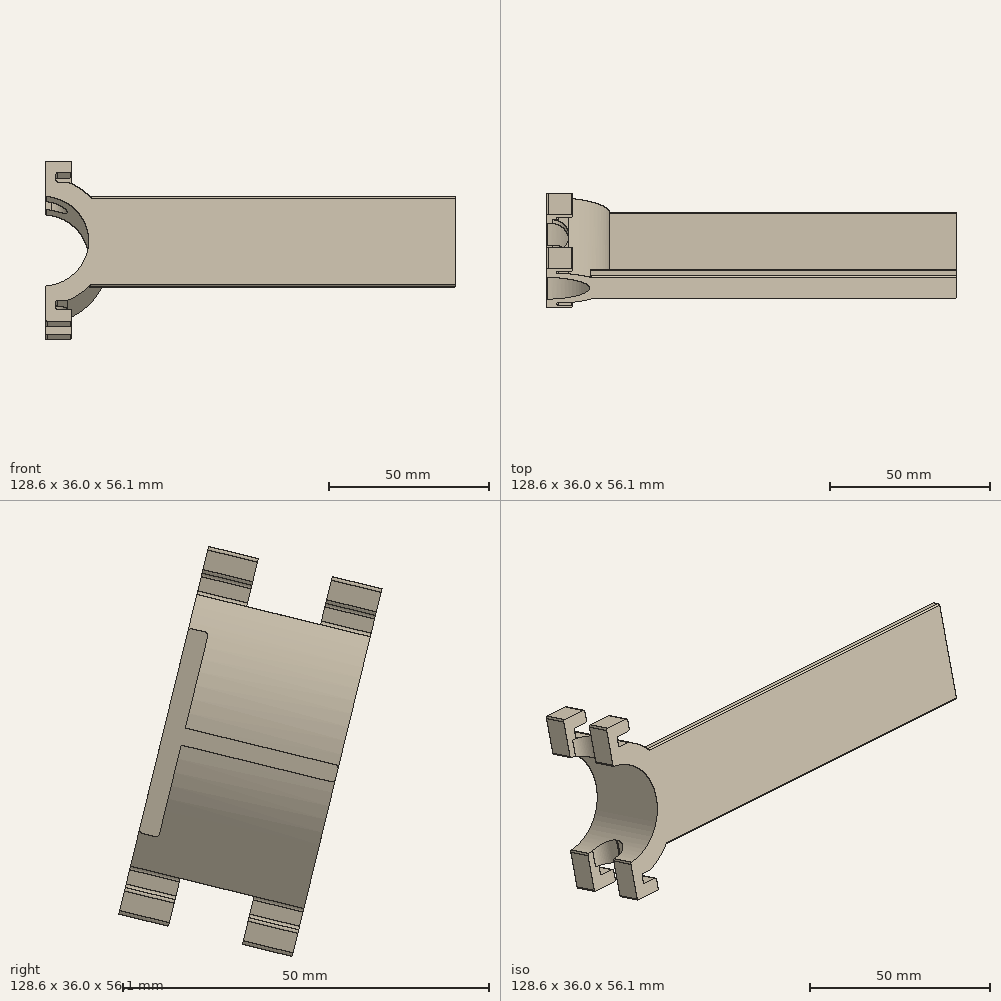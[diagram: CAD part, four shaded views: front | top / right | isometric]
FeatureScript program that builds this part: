
annotation { "Feature Type Name" : "Feature", "Feature Type Description" : "" }
export const myFeature = defineFeature(function(context is Context, id is Id, definition is map)
    precondition{}
    {
        {
            var Q0;
            Q0=qCreatedBy(makeId("Right.planeOp"),FACE);
            var sketch = newSketch(context, id + "F0", { "sketchPlane" : qUnion([Q0])});
            skLineSegment(sketch, "E0.0", {"start": v(15.97, -2.87) * mm, "end": v(15.4, -5.2) * mm});
            skLineSegment(sketch, "E0.1", {"start": v(15.4, -5.2) * mm, "end": v(-5.58, -0.08) * mm});
            skLineSegment(sketch, "E0.2", {"start": v(15.97, -2.87) * mm, "end": v(-5, 2.25) * mm});
            skLineSegment(sketch, "E0.3", {"start": v(-5.58, -0.08) * mm, "end": v(-8.66, -12.7) * mm});
            skLineSegment(sketch, "E0.4", {"start": v(-11.38, -12.04) * mm, "end": v(-8.66, -12.7) * mm});
            skLineSegment(sketch, "E0.5", {"start": v(-8.32, 0.49) * mm, "end": v(-11.38, -12.04) * mm});
            skLineSegment(sketch, "E0.6", {"start": v(-1.83, 15.27) * mm, "end": v(-5, 2.25) * mm});
            skLineSegment(sketch, "E0.7", {"start": v(-4.55, 15.93) * mm, "end": v(-1.83, 15.27) * mm});
            skLineSegment(sketch, "E0.8", {"start": v(-4.55, 15.93) * mm, "end": v(-7.6, 3.4) * mm});
            skLineSegment(sketch, "E0.9", {"start": v(-7.6, 3.4) * mm, "end": v(-8.32, 0.49) * mm});
            skSolve(sketch);
        }
        {
            var Q0;
            Q0=makeQuery(id+"F0.imprint","IMPRINT",FACE,{"disambiguationData":[TD([[makeQuery(id+"F0.imprint","IMPRINT",EDGE,{"derivedFrom":sQuery(id+"F0.wireOp",EDGE,"19673f29-938b-42fe-a6ce-3b0a3df10b1a.0")}),1.0]])]});
            var Q1;
            Q1=makeQuery(id+"F0.imprint","IMPRINT",FACE,{"disambiguationData":[TD([[makeQuery(id+"F0.imprint","IMPRINT",EDGE,{"derivedFrom":sQuery(id+"F0.wireOp",EDGE,"E0.0")}),-1.0]])]});
            extrude(context, id + "F1", {"entities" : qUnion([Q0, Q1]), "oppositeDirection" : true, "depth" : 115 * mm});
        }
        {
            var Q0;
            Q0=makeQuery(id+"F1.opExtrude","SWEPT_EDGE",EDGE,{"disambiguationData":[OSD([sQuery(id+"F0.wireOp",EDGE,"E0.0"),sQuery(id+"F0.wireOp",EDGE,"E0.1")])]});
            var Q1;
            Q1=makeQuery(id+"F1.opExtrude","SWEPT_EDGE",EDGE,{"disambiguationData":[OSD([sQuery(id+"F0.wireOp",EDGE,"E0.3"),sQuery(id+"F0.wireOp",EDGE,"E0.4")])]});
            var Q2;
            Q2=makeQuery(id+"F1.opExtrude","SWEPT_EDGE",EDGE,{"disambiguationData":[OSD([sQuery(id+"F0.wireOp",EDGE,"E0.4"),sQuery(id+"F0.wireOp",EDGE,"E0.5")])]});
            var Q3;
            Q3=makeQuery(id+"F1.opExtrude","SWEPT_EDGE",EDGE,{"disambiguationData":[OSD([sQuery(id+"F0.wireOp",EDGE,"E0.7"),sQuery(id+"F0.wireOp",EDGE,"E0.8")])]});
            var Q4;
            Q4=makeQuery(id+"F1.opExtrude","SWEPT_EDGE",EDGE,{"disambiguationData":[OSD([sQuery(id+"F0.wireOp",EDGE,"E0.6"),sQuery(id+"F0.wireOp",EDGE,"E0.7")])]});
            var Q5;
            Q5=makeQuery(id+"F1.opExtrude","SWEPT_EDGE",EDGE,{"disambiguationData":[OSD([sQuery(id+"F0.wireOp",EDGE,"E0.0"),sQuery(id+"F0.wireOp",EDGE,"E0.2")])]});
            fillet(context, id + "F2", {"entities" : qUnion([Q0, Q1, Q2, Q3, Q4, Q5]), "radius" : 0.5 * mm, "tangentPropagation" : true, "allowEdgeOverflow" : false});
        }
        {
            var Q0;
            Q0=makeQuery(id+"F1.opExtrude","SWEPT_FACE",FACE,{"disambiguationData":[OSD([sQuery(id+"F0.wireOp",EDGE,"E0.5"),sQuery(id+"F0.wireOp",EDGE,"E0.8"),sQuery(id+"F0.wireOp",EDGE,"E0.9")])]});
            var sketch = newSketch(context, id + "F3", { "sketchPlane" : qUnion([Q0])});
            skArc(sketch, "E1", {"start": v(-128.56, -14.47) * mm, "mid": v(-115, 0) * mm, "end": v(-128.56, 14.47) * mm});
            skPoint(sketch, "E1.centerSnap0", {"position": v(-115, 0) * mm});
            skLineSegment(sketch, "E2.right", {"start": v(-128.56, 25.87) * mm, "end": v(-128.56, 14.47) * mm});
            skLineSegment(sketch, "E3", {"start": v(-128.56, 25.87) * mm, "end": v(-120.27, 25.87) * mm});
            skLineSegment(sketch, "E4", {"start": v(-121.58, 19.12) * mm, "end": v(-125.27, 19.12) * mm});
            skLineSegment(sketch, "E5", {"start": v(-125.27, 19.12) * mm, "end": v(-125.27, 22.12) * mm});
            skLineSegment(sketch, "E6", {"start": v(-125.27, 22.12) * mm, "end": v(-120.27, 22.12) * mm});
            skLineSegment(sketch, "E7", {"start": v(-120.27, 25.87) * mm, "end": v(-120.27, 22.12) * mm});
            skLineSegment(sketch, "E8.MirrorCS", {"start": v(-125.27, -19.12) * mm, "end": v(-125.27, -22.12) * mm});
            skLineSegment(sketch, "E9.MirrorCS", {"start": v(-121.58, -19.12) * mm, "end": v(-125.27, -19.12) * mm});
            skLineSegment(sketch, "E10.MirrorCS", {"start": v(-120.27, -25.87) * mm, "end": v(-120.27, -22.12) * mm});
            skLineSegment(sketch, "E11.MirrorCS", {"start": v(-125.27, -22.12) * mm, "end": v(-120.27, -22.12) * mm});
            skLineSegment(sketch, "E12.MirrorCS", {"start": v(-128.56, -25.87) * mm, "end": v(-120.27, -25.87) * mm});
            skArc(sketch, "E13.trimOffspring", {"start": v(-121.58, -19.12) * mm, "mid": v(-108.8, 0) * mm, "end": v(-121.58, 19.12) * mm});
            skLineSegment(sketch, "E14.trimOffspring", {"start": v(-128.56, -14.47) * mm, "end": v(-128.56, -25.87) * mm});
            skSolve(sketch);
        }
        {
            var Q0;
            {var subQ1=sQuery(id+"F3.wireOp",EDGE,"E2.right");Q0=makeQuery(id+"F3.imprint","IMPRINT",FACE,{"disambiguationData":[TD([[makeQuery(id+"F3.imprint","IMPRINT",EDGE,{"derivedFrom":subQ1}),1.0]])]});}
            var Q1;
            {var subQ0=sQuery(id+"F0.wireOp",EDGE,"E0.9");var subQ1=sQuery(id+"F0.wireOp",EDGE,"E0.8");var subQ2=sQuery(id+"F0.wireOp",EDGE,"E0.5");var subQ4=makeQuery(id+"F1.opExtrude","SWEPT_FACE",FACE,{"disambiguationData":[OSD([subQ2,subQ1,subQ0])]});var subQ5=makeQuery(id+"F2.opFillet","BLEND_EDGE",EDGE,{"blendedFrom":[makeQuery(id+"F1.opExtrude","SWEPT_EDGE",EDGE,{"disambiguationData":[OSD([sQuery(id+"F0.wireOp",EDGE,"E0.4"),subQ2])]}),subQ4],"blendedInto":[subQ4]});var subQ10=sQuery(id+"F3.wireOp",EDGE,"E13.trimOffspring");var subQ12=makeQuery(id+"F3.imprint","INTERSECT",VERTEX,{"derivedFrom":[subQ5,subQ10]});Q1=makeQuery(id+"F3.imprint","IMPRINT",FACE,{"disambiguationData":[TD([[makeQuery(id+"F3.imprint","IMPRINT",EDGE,{"disambiguationData":[TD([[subQ12,-1.0]])],"derivedFrom":subQ10}),1.0]])]});}
            var Q2;
            Q2=makeQuery(id+"F3.imprint","IMPRINT",FACE,{"disambiguationData":[TD([[makeQuery(id+"F3.imprint","IMPRINT",EDGE,{"derivedFrom":sQuery(id+"F3.wireOp",EDGE,"E8.MirrorCS")}),-1.0]])]});
            extrude(context, id + "F4", {"entities" : qUnion([Q0, Q1, Q2]), "operationType" : NewBodyOperationType.ADD, "oppositeDirection" : true, "depth" : 24.4 * mm});
        }
        {
            var Q0;
            Q0=makeQuery(id+"F4.opExtrude","SWEPT_EDGE",EDGE,{"disambiguationData":[OSD([sQuery(id+"F3.wireOp",EDGE,"E3"),sQuery(id+"F3.wireOp",EDGE,"E7")])]});
            var Q1;
            Q1=makeQuery(id+"F4.opExtrude","SWEPT_EDGE",EDGE,{"disambiguationData":[OSD([sQuery(id+"F3.wireOp",EDGE,"E6"),sQuery(id+"F3.wireOp",EDGE,"E7")])]});
            var Q2;
            Q2=makeQuery(id+"F4.opExtrude","SWEPT_EDGE",EDGE,{"disambiguationData":[OSD([sQuery(id+"F3.wireOp",EDGE,"E5"),sQuery(id+"F3.wireOp",EDGE,"E6")])]});
            var Q3;
            Q3=makeQuery(id+"F4.opExtrude","SWEPT_EDGE",EDGE,{"disambiguationData":[OSD([sQuery(id+"F3.wireOp",EDGE,"E4"),sQuery(id+"F3.wireOp",EDGE,"E5")])]});
            var Q4;
            Q4=makeQuery(id+"F4.opExtrude","SWEPT_EDGE",EDGE,{"disambiguationData":[OSD([sQuery(id+"F3.wireOp",EDGE,"E8.MirrorCS"),sQuery(id+"F3.wireOp",EDGE,"E9.MirrorCS")])]});
            var Q5;
            Q5=makeQuery(id+"F4.opExtrude","SWEPT_EDGE",EDGE,{"disambiguationData":[OSD([sQuery(id+"F3.wireOp",EDGE,"E8.MirrorCS"),sQuery(id+"F3.wireOp",EDGE,"E11.MirrorCS")])]});
            var Q6;
            Q6=makeQuery(id+"F4.opExtrude","SWEPT_EDGE",EDGE,{"disambiguationData":[OSD([sQuery(id+"F3.wireOp",EDGE,"E10.MirrorCS"),sQuery(id+"F3.wireOp",EDGE,"E11.MirrorCS")])]});
            var Q7;
            Q7=makeQuery(id+"F4.opExtrude","SWEPT_EDGE",EDGE,{"disambiguationData":[OSD([sQuery(id+"F3.wireOp",EDGE,"E10.MirrorCS"),sQuery(id+"F3.wireOp",EDGE,"E12.MirrorCS")])]});
            var Q8;
            Q8=makeQuery(id+"F4.opExtrude","SWEPT_EDGE",EDGE,{"disambiguationData":[OSD([sQuery(id+"F3.wireOp",EDGE,"E12.MirrorCS"),sQuery(id+"F3.wireOp",EDGE,"E14.trimOffspring")])]});
            var Q9;
            Q9=makeQuery(id+"F4.opExtrude","SWEPT_EDGE",EDGE,{"disambiguationData":[OSD([sQuery(id+"F3.wireOp",EDGE,"E1"),sQuery(id+"F3.wireOp",EDGE,"E14.trimOffspring")])]});
            var Q10;
            Q10=makeQuery(id+"F4.opExtrude","SWEPT_EDGE",EDGE,{"disambiguationData":[OSD([sQuery(id+"F3.wireOp",EDGE,"E1"),sQuery(id+"F3.wireOp",EDGE,"E2.right")])]});
            var Q11;
            Q11=makeQuery(id+"F4.opExtrude","SWEPT_EDGE",EDGE,{"disambiguationData":[OSD([sQuery(id+"F3.wireOp",EDGE,"E2.right"),sQuery(id+"F3.wireOp",EDGE,"E3")])]});
            fillet(context, id + "F5", {"entities" : qUnion([Q0, Q1, Q2, Q3, Q4, Q5, Q6, Q7, Q8, Q9, Q10, Q11]), "radius" : .5 * mm, "tangentPropagation" : true, "allowEdgeOverflow" : false});
        }
        {
            var Q0;
            Q0=makeQuery(id+"F4.opExtrude","SWEPT_FACE",FACE,{"disambiguationData":[OSD([sQuery(id+"F3.wireOp",EDGE,"E2.right")])]});
            var sketch = newSketch(context, id + "F6", { "sketchPlane" : qUnion([Q0])});
            skLineSegment(sketch, "E15.0", {"start": v(-14.96, 22.46) * mm, "end": v(-12.48, 12.33) * mm});
            skLineSegment(sketch, "E16.0", {"start": v(5.7, -18.3) * mm, "end": v(-3.37, 18.86) * mm});
            skLineSegment(sketch, "E17", {"start": v(-12.48, 12.33) * mm, "end": v(0.6, -41.2) * mm});
            skLineSegment(sketch, "E18", {"start": v(5.7, -18.3) * mm, "end": v(10.7, -38.73) * mm});
            skLineSegment(sketch, "E19", {"start": v(-3.37, 18.86) * mm, "end": v(-6.55, 31.86) * mm});
            skLineSegment(sketch, "E20", {"start": v(-14.96, 22.46) * mm, "end": v(-16.68, 29.5) * mm});
            skLineSegment(sketch, "E21", {"start": v(-16.68, 29.5) * mm, "end": v(-6.55, 31.86) * mm});
            skLineSegment(sketch, "E22", {"start": v(10.7, -38.73) * mm, "end": v(0.6, -41.2) * mm});
            skSolve(sketch);
        }
        {
            var Q0;
            {var subQ0=sQuery(id+"F6.wireOp",EDGE,"E18");Q0=makeQuery(id+"F6.imprint","IMPRINT",FACE,{"disambiguationData":[TD([[makeQuery(id+"F6.imprint","IMPRINT",EDGE,{"derivedFrom":subQ0}),-1.0]])]});}
            var Q1;
            {var subQ8=sQuery(id+"F6.wireOp",EDGE,"E15.0");Q1=makeQuery(id+"F6.imprint","IMPRINT",FACE,{"disambiguationData":[TD([[makeQuery(id+"F6.imprint","IMPRINT",EDGE,{"derivedFrom":subQ8}),1.0]])]});}
            var Q2;
            {var subQ0=sQuery(id+"F6.wireOp",EDGE,"E21");Q2=makeQuery(id+"F6.imprint","IMPRINT",FACE,{"disambiguationData":[TD([[makeQuery(id+"F6.imprint","IMPRINT",EDGE,{"derivedFrom":subQ0}),-1.0]])]});}
            extrude(context, id + "F7", {"entities" : qUnion([Q0, Q1, Q2]), "operationType" : NewBodyOperationType.REMOVE, "oppositeDirection" : true, "depth" : 7 * mm});
        }
        {
            var Q0;
            {var subQ0=sQuery(id+"F6.wireOp",EDGE,"E20");var subQ1=sQuery(id+"F6.wireOp",EDGE,"E17");var subQ2=sQuery(id+"F6.wireOp",EDGE,"E15.0");Q0=makeQuery(id+"F7.boolean.opBoolean","COPY",EDGE,{"disambiguationData":[TD([makeQuery(id+"F4.opExtrude","SWEPT_FACE",FACE,{"disambiguationData":[OSD([sQuery(id+"F3.wireOp",EDGE,"E1")])]}),makeQuery(id+"F4.opExtrude","SWEPT_FACE",FACE,{"disambiguationData":[OSD([sQuery(id+"F3.wireOp",EDGE,"E13.trimOffspring")])]}),makeQuery(id+"F7.opExtrude","CAP_FACE",FACE,{"disambiguationData":[OSD([subQ2,sQuery(id+"F6.wireOp",EDGE,"E16.0"),subQ1,sQuery(id+"F6.wireOp",EDGE,"E18"),sQuery(id+"F6.wireOp",EDGE,"E19"),subQ0,sQuery(id+"F6.wireOp",EDGE,"E21"),sQuery(id+"F6.wireOp",EDGE,"E22")])],"isStart":false}),makeQuery(id+"F7.opExtrude","SWEPT_FACE",FACE,{"disambiguationData":[OSD([subQ2,subQ1,subQ0])]})]),OD(1.0)],"derivedFrom":makeQuery(id+"F7.opExtrude","CAP_EDGE",EDGE,{"disambiguationData":[OSD([subQ2,subQ1,subQ0])],"isStart":false})});}
            var Q1;
            {var subQ0=sQuery(id+"F6.wireOp",EDGE,"E19");var subQ1=sQuery(id+"F6.wireOp",EDGE,"E18");var subQ2=sQuery(id+"F6.wireOp",EDGE,"E16.0");Q1=makeQuery(id+"F7.boolean.opBoolean","COPY",EDGE,{"disambiguationData":[TD([makeQuery(id+"F4.opExtrude","SWEPT_FACE",FACE,{"disambiguationData":[OSD([sQuery(id+"F3.wireOp",EDGE,"E1")])]}),makeQuery(id+"F4.opExtrude","SWEPT_FACE",FACE,{"disambiguationData":[OSD([sQuery(id+"F3.wireOp",EDGE,"E13.trimOffspring")])]}),makeQuery(id+"F7.opExtrude","CAP_FACE",FACE,{"disambiguationData":[OSD([sQuery(id+"F6.wireOp",EDGE,"E15.0"),subQ2,sQuery(id+"F6.wireOp",EDGE,"E17"),subQ1,subQ0,sQuery(id+"F6.wireOp",EDGE,"E20"),sQuery(id+"F6.wireOp",EDGE,"E21"),sQuery(id+"F6.wireOp",EDGE,"E22")])],"isStart":false}),makeQuery(id+"F7.opExtrude","SWEPT_FACE",FACE,{"disambiguationData":[OSD([subQ2,subQ1,subQ0])]})]),OD(1.0)],"derivedFrom":makeQuery(id+"F7.opExtrude","CAP_EDGE",EDGE,{"disambiguationData":[OSD([subQ2,subQ1,subQ0])],"isStart":false})});}
            var Q2;
            {var subQ0=sQuery(id+"F6.wireOp",EDGE,"E20");var subQ1=sQuery(id+"F6.wireOp",EDGE,"E17");var subQ2=sQuery(id+"F6.wireOp",EDGE,"E15.0");Q2=makeQuery(id+"F7.boolean.opBoolean","COPY",EDGE,{"disambiguationData":[TD([makeQuery(id+"F4.opExtrude","SWEPT_FACE",FACE,{"disambiguationData":[OSD([sQuery(id+"F3.wireOp",EDGE,"E1")])]}),makeQuery(id+"F4.opExtrude","SWEPT_FACE",FACE,{"disambiguationData":[OSD([sQuery(id+"F3.wireOp",EDGE,"E13.trimOffspring")])]}),makeQuery(id+"F7.opExtrude","CAP_FACE",FACE,{"disambiguationData":[OSD([subQ2,sQuery(id+"F6.wireOp",EDGE,"E16.0"),subQ1,sQuery(id+"F6.wireOp",EDGE,"E18"),sQuery(id+"F6.wireOp",EDGE,"E19"),subQ0,sQuery(id+"F6.wireOp",EDGE,"E21"),sQuery(id+"F6.wireOp",EDGE,"E22")])],"isStart":false}),makeQuery(id+"F7.opExtrude","SWEPT_FACE",FACE,{"disambiguationData":[OSD([subQ2,subQ1,subQ0])]})]),OD(0.0)],"derivedFrom":makeQuery(id+"F7.opExtrude","CAP_EDGE",EDGE,{"disambiguationData":[OSD([subQ2,subQ1,subQ0])],"isStart":false})});}
            var Q3;
            {var subQ0=sQuery(id+"F6.wireOp",EDGE,"E19");var subQ1=sQuery(id+"F6.wireOp",EDGE,"E18");var subQ2=sQuery(id+"F6.wireOp",EDGE,"E16.0");Q3=makeQuery(id+"F7.boolean.opBoolean","COPY",EDGE,{"disambiguationData":[TD([makeQuery(id+"F4.opExtrude","SWEPT_FACE",FACE,{"disambiguationData":[OSD([sQuery(id+"F3.wireOp",EDGE,"E1")])]}),makeQuery(id+"F4.opExtrude","SWEPT_FACE",FACE,{"disambiguationData":[OSD([sQuery(id+"F3.wireOp",EDGE,"E13.trimOffspring")])]}),makeQuery(id+"F7.opExtrude","CAP_FACE",FACE,{"disambiguationData":[OSD([sQuery(id+"F6.wireOp",EDGE,"E15.0"),subQ2,sQuery(id+"F6.wireOp",EDGE,"E17"),subQ1,subQ0,sQuery(id+"F6.wireOp",EDGE,"E20"),sQuery(id+"F6.wireOp",EDGE,"E21"),sQuery(id+"F6.wireOp",EDGE,"E22")])],"isStart":false}),makeQuery(id+"F7.opExtrude","SWEPT_FACE",FACE,{"disambiguationData":[OSD([subQ2,subQ1,subQ0])]})]),OD(0.0)],"derivedFrom":makeQuery(id+"F7.opExtrude","CAP_EDGE",EDGE,{"disambiguationData":[OSD([subQ2,subQ1,subQ0])],"isStart":false})});}
            fillet(context, id + "F8", {"entities" : qUnion([Q0, Q1, Q2, Q3]), "radius" : 5 * mm, "tangentPropagation" : true, "allowEdgeOverflow" : false});
        }
        {
            var Q0;
            Q0=makeQuery(id+"F4.opExtrude","SWEPT_FACE",FACE,{"disambiguationData":[OSD([sQuery(id+"F3.wireOp",EDGE,"E12.MirrorCS")])]});
            var sketch = newSketch(context, id + "F9", { "sketchPlane" : qUnion([Q0])});
            skLineSegment(sketch, "E23", {"start": v(-128.06, -9.2) * mm, "end": v(-117.2, -9.2) * mm});
            skLineSegment(sketch, "E24", {"start": v(-117.2, -9.2) * mm, "end": v(-117.2, 1.2) * mm});
            skLineSegment(sketch, "E25", {"start": v(-117.2, 1.2) * mm, "end": v(-128.06, 1.2) * mm});
            skLineSegment(sketch, "E26", {"start": v(-128.06, 1.2) * mm, "end": v(-130.12, 1.2) * mm});
            skLineSegment(sketch, "E27", {"start": v(-130.12, 1.2) * mm, "end": v(-130.12, -9.2) * mm});
            skLineSegment(sketch, "E28", {"start": v(-130.12, -9.2) * mm, "end": v(-128.06, -9.2) * mm});
            skSolve(sketch);
        }
        {
            var Q0;
            {var subQ0=sQuery(id+"F9.wireOp",EDGE,"E24");Q0=makeQuery(id+"F9.imprint","IMPRINT",FACE,{"disambiguationData":[TD([[makeQuery(id+"F9.imprint","IMPRINT",EDGE,{"derivedFrom":subQ0}),1.0]])]});}
            var Q1;
            {var subQ0=sQuery(id+"F3.wireOp",EDGE,"E12.MirrorCS");var subQ1=makeQuery(id+"F4.opExtrude","SWEPT_FACE",FACE,{"disambiguationData":[OSD([subQ0])]});var subQ2=subQ1;var subQ6=sQuery(id+"F6.wireOp",EDGE,"E20");var subQ7=sQuery(id+"F6.wireOp",EDGE,"E19");var subQ8=sQuery(id+"F6.wireOp",EDGE,"E18");var subQ9=sQuery(id+"F6.wireOp",EDGE,"E17");var subQ10=sQuery(id+"F6.wireOp",EDGE,"E16.0");var subQ11=sQuery(id+"F6.wireOp",EDGE,"E15.0");var subQ12=makeQuery(id+"F7.opExtrude","CAP_FACE",FACE,{"disambiguationData":[OSD([subQ11,subQ10,subQ9,subQ8,subQ7,subQ6,sQuery(id+"F6.wireOp",EDGE,"E21"),sQuery(id+"F6.wireOp",EDGE,"E22")])],"isStart":false});Q1=makeQuery(id+"F9.imprint","IMPRINT",FACE,{"disambiguationData":[TD([[makeQuery(id+"F9.imprint","IMPRINT",EDGE,{"derivedFrom":makeQuery(id+"F7.boolean.opBoolean","INTERSECT",EDGE,{"derivedFrom":[subQ2,subQ12]})}),1.0]])]});}
            extrude(context, id + "F10", {"entities" : qUnion([Q0, Q1]), "operationType" : NewBodyOperationType.REMOVE, "oppositeDirection" : true, "depth" : 6.75 * mm});
        }
        {
            var Q0;
            Q0=makeQuery(id+"F4.opExtrude","SWEPT_FACE",FACE,{"disambiguationData":[OSD([sQuery(id+"F3.wireOp",EDGE,"E3")])]});
            var sketch = newSketch(context, id + "F11", { "sketchPlane" : qUnion([Q0])});
            skLineSegment(sketch, "E29", {"start": v(-128.06, -1.2) * mm, "end": v(-118.96, -1.2) * mm});
            skLineSegment(sketch, "E30", {"start": v(-118.96, -1.2) * mm, "end": v(-118.96, 9.2) * mm});
            skLineSegment(sketch, "E31", {"start": v(-118.96, 9.2) * mm, "end": v(-128.06, 9.2) * mm});
            skLineSegment(sketch, "E32", {"start": v(-130.9, 9.2) * mm, "end": v(-130.9, -1.2) * mm});
            skLineSegment(sketch, "E33", {"start": v(-130.9, -1.2) * mm, "end": v(-128.06, -1.2) * mm});
            skLineSegment(sketch, "E34", {"start": v(-130.9, 9.2) * mm, "end": v(-128.06, 9.2) * mm});
            skSolve(sketch);
        }
        {
            var Q0;
            Q0=makeQuery(id+"F11.imprint","IMPRINT",FACE,{"disambiguationData":[TD([[makeQuery(id+"F11.imprint","IMPRINT",EDGE,{"derivedFrom":sQuery(id+"F11.wireOp",EDGE,"E32")}),1.0]])]});
            var Q1;
            {var subQ0=sQuery(id+"F6.wireOp",EDGE,"E20");var subQ1=sQuery(id+"F6.wireOp",EDGE,"E19");var subQ2=sQuery(id+"F6.wireOp",EDGE,"E18");var subQ3=sQuery(id+"F6.wireOp",EDGE,"E17");var subQ4=sQuery(id+"F6.wireOp",EDGE,"E16.0");var subQ5=sQuery(id+"F6.wireOp",EDGE,"E15.0");var subQ6=makeQuery(id+"F7.opExtrude","CAP_FACE",FACE,{"disambiguationData":[OSD([subQ5,subQ4,subQ3,subQ2,subQ1,subQ0,sQuery(id+"F6.wireOp",EDGE,"E21"),sQuery(id+"F6.wireOp",EDGE,"E22")])],"isStart":false});var subQ7=sQuery(id+"F3.wireOp",EDGE,"E3");var subQ8=makeQuery(id+"F4.opExtrude","SWEPT_FACE",FACE,{"disambiguationData":[OSD([subQ7])]});var subQ9=subQ8;Q1=makeQuery(id+"F11.imprint","IMPRINT",FACE,{"disambiguationData":[TD([[makeQuery(id+"F11.imprint","IMPRINT",EDGE,{"derivedFrom":makeQuery(id+"F7.boolean.opBoolean","INTERSECT",EDGE,{"derivedFrom":[subQ9,subQ6]})}),-1.0]])]});}
            var Q2;
            {var subQ0=sQuery(id+"F11.wireOp",EDGE,"E30");Q2=makeQuery(id+"F11.imprint","IMPRINT",FACE,{"disambiguationData":[TD([[makeQuery(id+"F11.imprint","IMPRINT",EDGE,{"derivedFrom":subQ0}),1.0]])]});}
            extrude(context, id + "F12", {"entities" : qUnion([Q0, Q1, Q2]), "operationType" : NewBodyOperationType.REMOVE, "oppositeDirection" : true, "depth" : 6.75 * mm});
        }
    });
